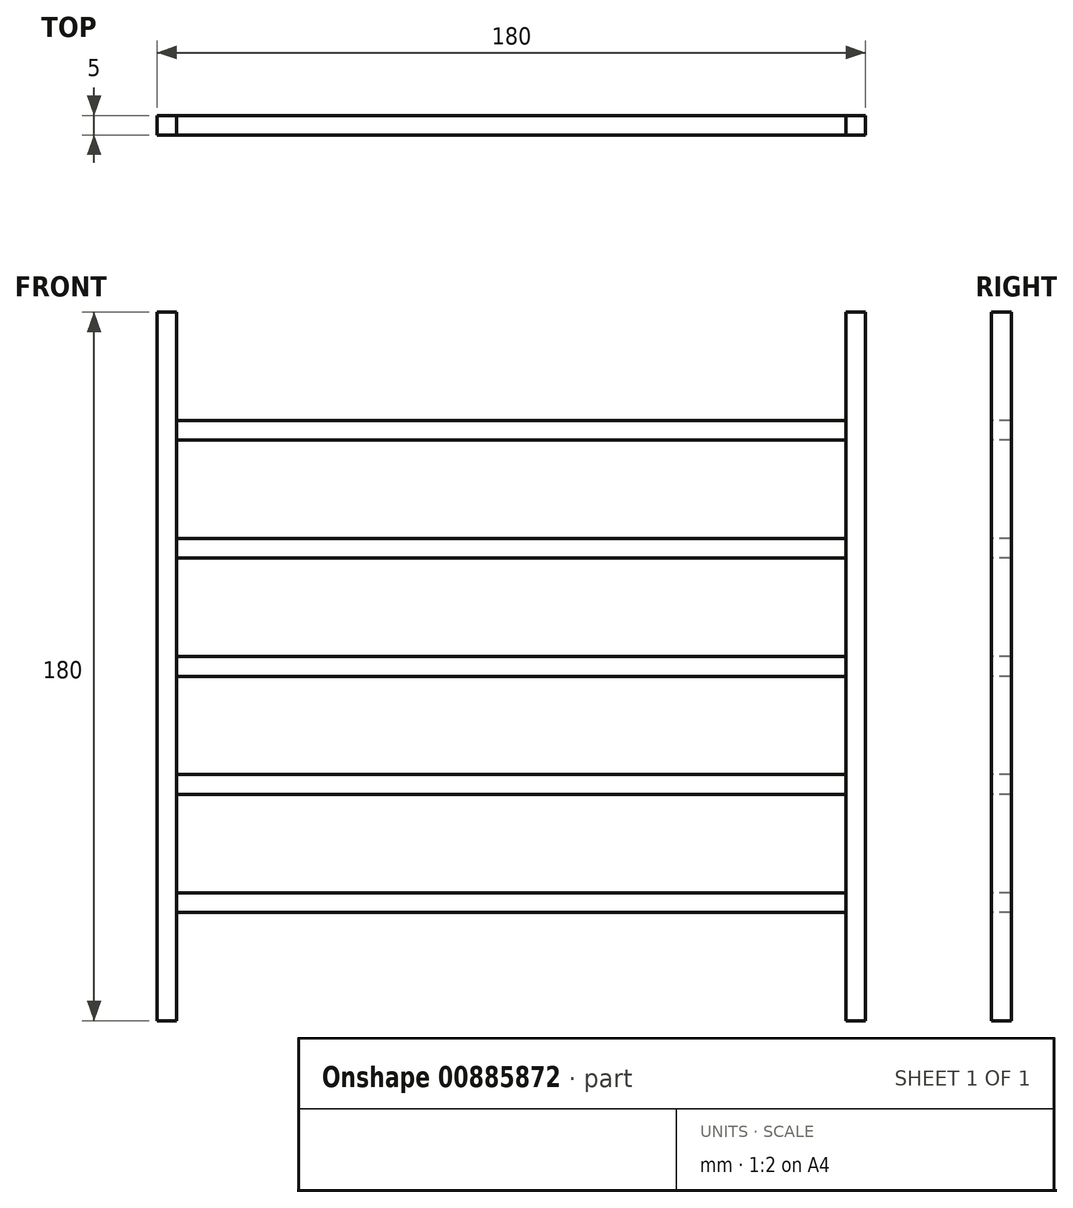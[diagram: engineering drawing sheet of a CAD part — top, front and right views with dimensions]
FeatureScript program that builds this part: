
annotation { "Feature Type Name" : "Feature", "Feature Type Description" : "" }
export const myFeature = defineFeature(function(context is Context, id is Id, definition is map)
    precondition{}
    {
        {
            var Q0;
            Q0=qCreatedBy(makeId("Top.planeOp"),FACE);
            var sketch = newSketch(context, id + "F0", { "sketchPlane" : qUnion([Q0])});
            skLineSegment(sketch, "E0.bottom", {"start": v(0, 0) * mm, "end": v(5, 0) * mm});
            skLineSegment(sketch, "E0.top", {"start": v(0, -5) * mm, "end": v(5, -5) * mm});
            skLineSegment(sketch, "E0.left", {"start": v(0, 0) * mm, "end": v(0, -5) * mm});
            skLineSegment(sketch, "E0.right", {"start": v(5, 0) * mm, "end": v(5, -5) * mm});
            skPoint(sketch, "E1.oppositeSnap0", {"position": v(2.5, -5) * mm});
            skLineSegment(sketch, "E1.bottom", {"start": v(175, 0) * mm, "end": v(180, 0) * mm});
            skLineSegment(sketch, "E1.top", {"start": v(175, -5) * mm, "end": v(180, -5) * mm});
            skLineSegment(sketch, "E1.left", {"start": v(175, 0) * mm, "end": v(175, -5) * mm});
            skLineSegment(sketch, "E1.right", {"start": v(180, 0) * mm, "end": v(180, -5) * mm});
            skSolve(sketch);
        }
        {
            var Q0;
            Q0 = qSketchRegion(id + "F0", true);
            extrude(context, id + "F1", {"entities" : qUnion([Q0]), "depth" : 180 * mm, "offsetDistance" : 25 * mm});
        }
        {
            var Q0;
            Q0=makeQuery(id+"F1.opExtrude","SWEPT_FACE",FACE,{"disambiguationData":[OSD([sQuery(id+"F0.wireOp",EDGE,"E0.right")])]});
            var sketch = newSketch(context, id + "F2", { "sketchPlane" : qUnion([Q0])});
            skLineSegment(sketch, "E2.bottom", {"start": v(0, 27.5) * mm, "end": v(-5, 27.5) * mm});
            skLineSegment(sketch, "E2.top", {"start": v(0, 32.5) * mm, "end": v(-5, 32.5) * mm});
            skLineSegment(sketch, "E2.left", {"start": v(0, 27.5) * mm, "end": v(0, 32.5) * mm});
            skLineSegment(sketch, "E2.right", {"start": v(-5, 27.5) * mm, "end": v(-5, 32.5) * mm});
            skLineSegment(sketch, "E3.bottom", {"start": v(0, 57.5) * mm, "end": v(-5, 57.5) * mm});
            skLineSegment(sketch, "E3.top", {"start": v(0, 62.5) * mm, "end": v(-5, 62.5) * mm});
            skLineSegment(sketch, "E3.left", {"start": v(0, 57.5) * mm, "end": v(0, 62.5) * mm});
            skLineSegment(sketch, "E3.right", {"start": v(-5, 57.5) * mm, "end": v(-5, 62.5) * mm});
            skLineSegment(sketch, "E4.bottom", {"start": v(0, 87.5) * mm, "end": v(-5, 87.5) * mm});
            skLineSegment(sketch, "E4.top", {"start": v(0, 92.5) * mm, "end": v(-5, 92.5) * mm});
            skLineSegment(sketch, "E4.left", {"start": v(0, 87.5) * mm, "end": v(0, 92.5) * mm});
            skLineSegment(sketch, "E4.right", {"start": v(-5, 87.5) * mm, "end": v(-5, 92.5) * mm});
            skLineSegment(sketch, "E5.bottom", {"start": v(0, 117.5) * mm, "end": v(-5, 117.5) * mm});
            skLineSegment(sketch, "E5.top", {"start": v(0, 122.5) * mm, "end": v(-5, 122.5) * mm});
            skLineSegment(sketch, "E5.left", {"start": v(0, 117.5) * mm, "end": v(0, 122.5) * mm});
            skLineSegment(sketch, "E5.right", {"start": v(-5, 117.5) * mm, "end": v(-5, 122.5) * mm});
            skLineSegment(sketch, "E6.bottom", {"start": v(0, 147.5) * mm, "end": v(-5, 147.5) * mm});
            skLineSegment(sketch, "E6.top", {"start": v(0, 152.5) * mm, "end": v(-5, 152.5) * mm});
            skLineSegment(sketch, "E6.left", {"start": v(0, 147.5) * mm, "end": v(0, 152.5) * mm});
            skLineSegment(sketch, "E6.right", {"start": v(-5, 147.5) * mm, "end": v(-5, 152.5) * mm});
            skSolve(sketch);
        }
        {
            var Q0;
            Q0 = qSketchRegion(id + "F2", true);
            extrude(context, id + "F3", {"entities" : qUnion([Q0]), "depth" : 170 * mm, "offsetDistance" : 25 * mm});
        }
    });
